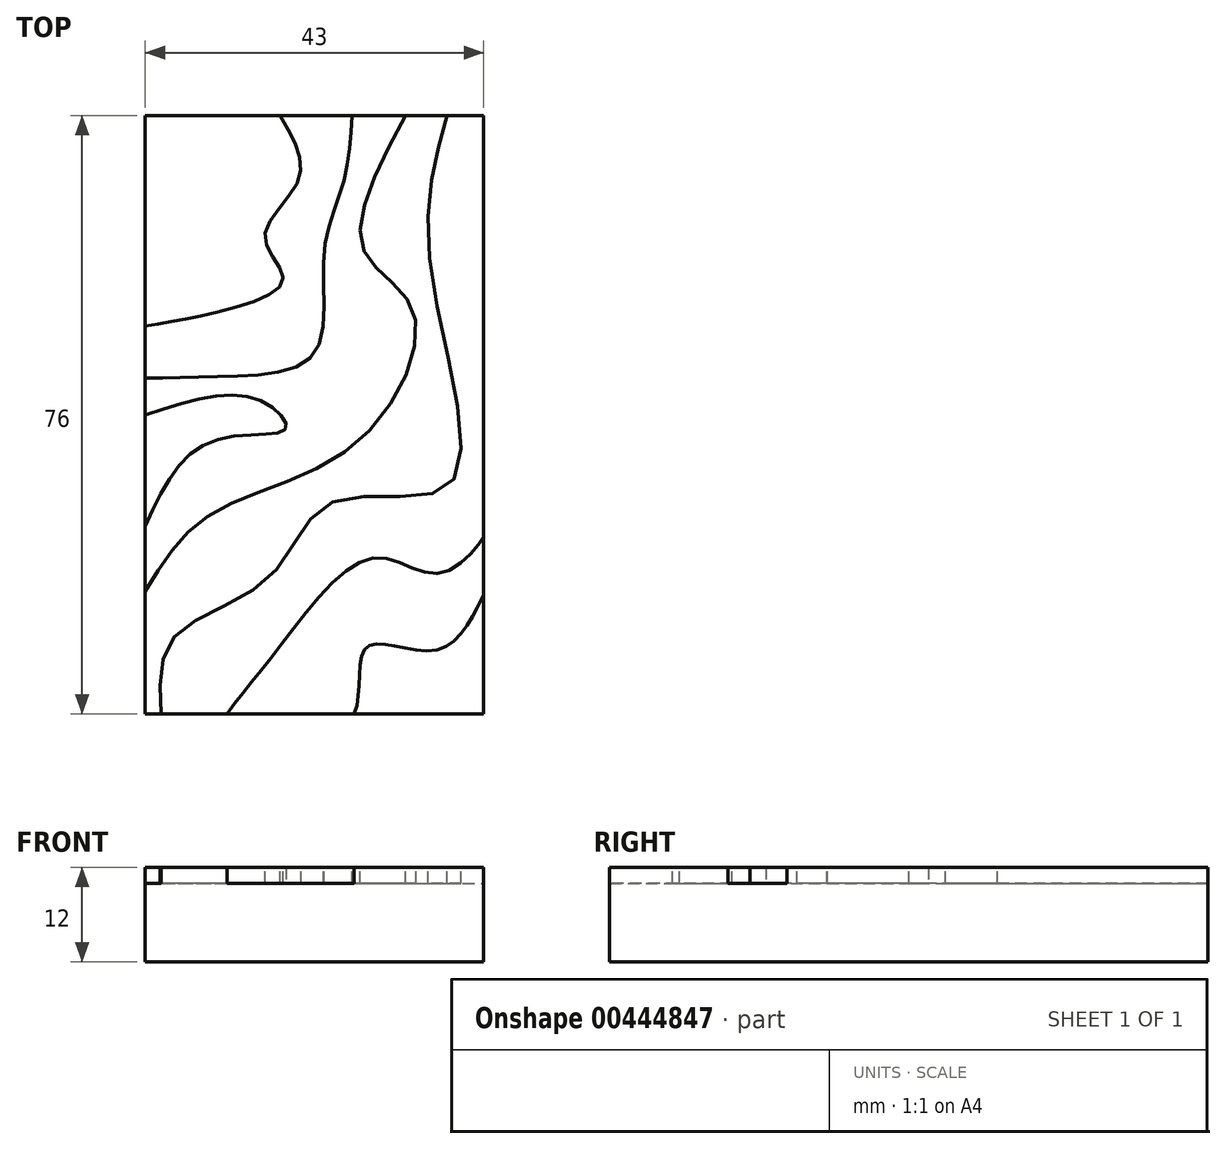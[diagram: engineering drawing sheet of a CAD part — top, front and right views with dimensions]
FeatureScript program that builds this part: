
annotation { "Feature Type Name" : "Feature", "Feature Type Description" : "" }
export const myFeature = defineFeature(function(context is Context, id is Id, definition is map)
    precondition{}
    {
        {
            var Q0;
            Q0=qCreatedBy(makeId("Top.planeOp"),FACE);
            var sketch = newSketch(context, id + "F0", { "sketchPlane" : qUnion([Q0])});
            skLineSegment(sketch, "E0.bottom", {"start": v(-21.5, 38) * mm, "end": v(21.5, 38) * mm});
            skLineSegment(sketch, "E0.top", {"start": v(-21.5, -38) * mm, "end": v(21.5, -38) * mm});
            skLineSegment(sketch, "E0.left", {"start": v(-21.5, 38) * mm, "end": v(-21.5, -38) * mm});
            skLineSegment(sketch, "E0.right", {"start": v(21.5, 38) * mm, "end": v(21.5, -38) * mm});
            skPoint(sketch, "E0.middle", {"position": v(0, 0) * mm});
            skSolve(sketch);
        }
        {
            var Q0;
            Q0=qSketchRegion(id+"F0",true);
            extrude(context, id + "F1", {"entities" : qUnion([Q0]), "depth" : 12 * mm});
        }
        {
            var Q0;
            Q0=makeQuery(id+"F1.opExtrude","CAP_FACE",FACE,{"disambiguationData":[OSD([sQuery(id+"F0.wireOp",EDGE,"E0.bottom"),sQuery(id+"F0.wireOp",EDGE,"E0.top"),sQuery(id+"F0.wireOp",EDGE,"E0.left"),sQuery(id+"F0.wireOp",EDGE,"E0.right")])],"isStart":false});
            var sketch = newSketch(context, id + "F2", { "sketchPlane" : qUnion([Q0])});
            skFitSpline(sketch, "E1", {"points": [v(-4.4, 38) * mm, v(-1.97, 29.98) * mm, v(-6.3, 22.6) * mm, v(-4.01, 17.13) * mm, v(-12.8, 12.92) * mm, v(-21.5, 11.27) * mm], "startDerivative": vector(24.57, -40.58) * mm, "endDerivative": vector(-37.33, -5.94) * mm});
            skFitSpline(sketch, "E2", {"points": [v(-21.5, 4.65) * mm, v(-10.5, 4.9) * mm, v(0, 7.83) * mm, v(1.2, 20.56) * mm, v(3.63, 29.35) * mm, v(4.77, 38) * mm], "startDerivative": vector(50.81, 0.95) * mm, "endDerivative": vector(3.2, 48.83) * mm});
            skFitSpline(sketch, "E3", {"points": [v(11.55, 38) * mm, v(6.18, 21.03) * mm, v(12.53, 13.2) * mm, v(5.22, -3.66) * mm, v(-13.05, -12.56) * mm, v(-21.5, -22.43) * mm], "startDerivative": vector(-48.65, -91.63) * mm, "endDerivative": vector(-36.91, -61.15) * mm});
            skFitSpline(sketch, "E4", {"points": [v(-21.5, 0) * mm, v(-7.15, 1.94) * mm, v(-3.69, -1.78) * mm, v(-12.92, -3.32) * mm, v(-21.5, -14.22) * mm], "startDerivative": vector(53.34, 17.24) * mm, "endDerivative": vector(-22.2, -48.51) * mm});
            skFitSpline(sketch, "E5", {"points": [v(-19.46, -38) * mm, v(-17.8, -28.2) * mm, v(-5.87, -20.76) * mm, v(2.47, -11.02) * mm, v(17.22, -8.84) * mm, v(14.78, 18.48) * mm, v(16.83, 38) * mm], "startDerivative": vector(-5.44, 83.83) * mm, "endDerivative": vector(25.52, 91.17) * mm});
            skFitSpline(sketch, "E6", {"points": [v(-11.13, -38) * mm, v(-4.33, -29.36) * mm, v(7.47, -18.2) * mm, v(15.93, -20.12) * mm, v(21.5, -15.5) * mm], "startDerivative": vector(22.35, 31.3) * mm, "endDerivative": vector(11.22, 17.57) * mm});
            skFitSpline(sketch, "E7", {"points": [v(5.03, -38) * mm, v(6.7, -29.48) * mm, v(16.06, -29.74) * mm, v(21.5, -22.94) * mm], "startDerivative": vector(10.43, 21.3) * mm, "endDerivative": vector(8.38, 13) * mm});
            skSolve(sketch);
        }
        {
            var Q0;
            Q0 = qSketchRegion(id + "F2", true);
            var Q1;
            {var subQ0=sQuery(id+"F2.wireOp",EDGE,"E1");Q1=makeQuery(id+"F2.imprint","IMPRINT",FACE,{"disambiguationData":[TD([[makeQuery(id+"F2.imprint","IMPRINT",EDGE,{"derivedFrom":subQ0}),1.0]])]});}
            var Q2;
            {var subQ0=sQuery(id+"F2.wireOp",EDGE,"E3");Q2=makeQuery(id+"F2.imprint","IMPRINT",FACE,{"disambiguationData":[TD([[makeQuery(id+"F2.imprint","IMPRINT",EDGE,{"derivedFrom":subQ0}),1.0]])]});}
            var Q3;
            {var subQ0=sQuery(id+"F2.wireOp",EDGE,"E4");Q3=makeQuery(id+"F2.imprint","IMPRINT",FACE,{"disambiguationData":[TD([[makeQuery(id+"F2.imprint","IMPRINT",EDGE,{"derivedFrom":subQ0}),-1.0]])]});}
            var Q4;
            {var subQ0=sQuery(id+"F2.wireOp",EDGE,"E6");Q4=makeQuery(id+"F2.imprint","IMPRINT",FACE,{"disambiguationData":[TD([[makeQuery(id+"F2.imprint","IMPRINT",EDGE,{"derivedFrom":subQ0}),-1.0]])]});}
            extrude(context, id + "F3", {"entities" : qUnion([Q0, Q1, Q2, Q3, Q4]), "operationType" : NewBodyOperationType.REMOVE, "oppositeDirection" : true, "depth" : 2 * mm});
        }
    });
